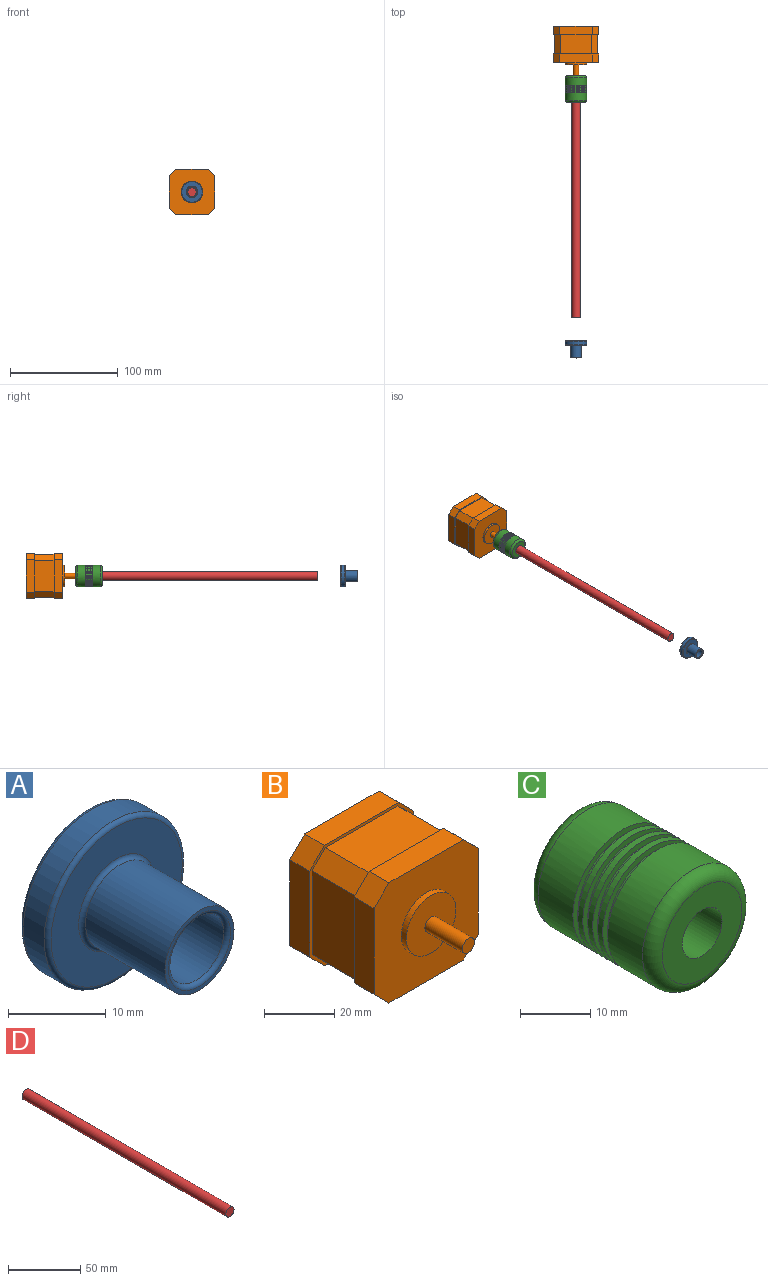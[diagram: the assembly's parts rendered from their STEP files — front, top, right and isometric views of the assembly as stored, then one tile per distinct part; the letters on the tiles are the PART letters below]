
ASSEMBLY  parts=4 mates=3
PART A: 10 faces, bbox 21.6x16x21.6 mm
  f0: cylinder r=4mm len=15.5mm, axis (0,-1,0), area 389.6mm2, adj f1,f9
  f1: plane 19x19mm, normal (0,1,0), area 233.3mm2, adj f0,f6
  f2: cylinder r=10mm len=20mm, axis (0,-1,0), area 188.5mm2, adj f6,f7
  f3: plane 19x19mm, normal (0,-1,0), area 188.5mm2, adj f7,f8
  f4: cylinder r=5mm len=11.5mm, axis (0,-1,0), area 361.3mm2, adj f5,f8
  f5: plane 10x10mm, normal (0,-1,0), area 14.9mm2, adj f4,f9
  f6: torus R=9.5mm, axis (0,-1,0), area 48.5mm2, adj f1,f2
  f7: torus R=9.5mm, axis (0,-1,0), area 48.5mm2, adj f2,f3
  f8: torus R=5.5mm, axis (0,-1,0), area 25.6mm2, adj f3,f4
  f9: torus R=4.5mm, axis (0,-1,0), area 20.6mm2, adj f0,f5
PART B: 32 faces, bbox 42x51x42 mm
  f0: plane 30x8mm, normal (0,0,-1), area 240mm2, adj f2,f3,f8,f18
  f1: plane 30x8mm, normal (1,0,0), area 240mm2, adj f3,f5,f8,f18
  f2: plane 8x6mm, normal (-0.71,0,-0.71), area 67.9mm2, adj f0,f6,f8,f18
  f3: plane 8x6mm, normal (0.71,0,-0.71), area 67.9mm2, adj f0,f1,f8,f18
  f4: plane 8x6mm, normal (-0.71,0,0.71), area 67.9mm2, adj f6,f7,f8,f18
  f5: plane 8x6mm, normal (0.71,0,0.71), area 67.9mm2, adj f1,f7,f8,f18
  f6: plane 30x8mm, normal (-1,0,0), area 240mm2, adj f2,f4,f8,f18
  f7: plane 30x8mm, normal (0,0,1), area 240mm2, adj f4,f5,f8,f18
  f8: plane 42x42mm, normal (0,-1,0), area 1377.8mm2, adj f0,f1,f2,f3,f4,f5,f6,f7
  f9: plane 18x5.41mm, normal (-0.71,0,0.71), area 137.8mm2, adj f10,f16,f17,f18
  f10: plane 29.17x18mm, normal (0,0,1), area 525.1mm2, adj f9,f11,f17,f18
  f11: plane 18x5.41mm, normal (0.71,0,0.71), area 137.8mm2, adj f10,f12,f17,f18
  f12: plane 29.17x18mm, normal (1,0,0), area 525.1mm2, adj f11,f13,f17,f18
  f13: plane 18x5.41mm, normal (0.71,0,-0.71), area 137.8mm2, adj f12,f14,f17,f18
  f14: plane 29.17x18mm, normal (0,0,-1), area 525.1mm2, adj f13,f15,f17,f18
  f15: plane 18x5.41mm, normal (-0.71,0,-0.71), area 137.8mm2, adj f14,f16,f17,f18
  f16: plane 29.17x18mm, normal (-1,0,0), area 525.1mm2, adj f9,f15,f17,f18
  f17: plane 42x42mm, normal (0,-1,0), area 150.6mm2, adj f9,f10,f11,f12,f13,f14,f15,f16
  f18: plane 42x42mm, normal (0,1,0), area 150.6mm2, adj f0,f1,f2,f3,f4,f5,f6,f7
  f19: plane 42x42mm, normal (0,1,0), area 1692mm2, adj f20,f21,f22,f23,f24,f25,f26,f27
  f20: plane 8x6mm, normal (-0.71,0,0.71), area 67.9mm2, adj f17,f19,f22,f27
  f21: plane 8x6mm, normal (0.71,0,0.71), area 67.9mm2, adj f17,f19,f22,f24
  f22: plane 30x8mm, normal (0,0,1), area 240mm2, adj f17,f19,f20,f21
  f23: plane 8x6mm, normal (0.71,0,-0.71), area 67.9mm2, adj f17,f19,f24,f26
  f24: plane 30x8mm, normal (1,0,0), area 240mm2, adj f17,f19,f21,f23
  f25: plane 8x6mm, normal (-0.71,0,-0.71), area 67.9mm2, adj f17,f19,f26,f27
  f26: plane 30x8mm, normal (0,0,-1), area 240mm2, adj f17,f19,f23,f25
  f27: plane 30x8mm, normal (-1,0,0), area 240mm2, adj f17,f19,f20,f25
  f28: cylinder r=10mm len=20mm, axis (0,1,0), area 125.7mm2, adj f8,f29
  f29: plane 20x20mm, normal (0,-1,0), area 294.5mm2, adj f28,f30
  f30: cylinder r=2.5mm len=15mm, axis (0,1,0), area 235.6mm2, adj f29,f31
  f31: plane 5x5mm, normal (0,-1,0), area 19.6mm2, adj f30
PART C: 24 faces, bbox 21.6x25x21.6 mm
  f0: cylinder r=2.5mm len=5mm, axis (0,-1,0), area 78.5mm2, adj f3,f22
  f1: cylinder r=10mm len=20mm, axis (0,-1,0), area 439.8mm2, adj f7,f21
  f2: cylinder r=10mm len=20mm, axis (0,-1,0), area 439.8mm2, adj f17,f20
  f3: plane 16x16mm, normal (0,1,0), area 181.4mm2, adj f0,f21
  f4: plane 16x16mm, normal (0,-1,0), area 150.8mm2, adj f20,f23
  f5: plane 20x20mm, normal (0,1,0), area 59.7mm2, adj f6,f8
  f6: cylinder r=9mm len=18mm, axis (0,1,0), area 56.5mm2, adj f5,f7
  f7: plane 20x20mm, normal (0,-1,0), area 59.7mm2, adj f1,f6
  f8: cylinder r=10mm len=20mm, axis (0,-1,0), area 62.8mm2, adj f5,f11
  f9: plane 20x20mm, normal (0,1,0), area 59.7mm2, adj f10,f12
  f10: cylinder r=9mm len=18mm, axis (0,1,0), area 56.5mm2, adj f9,f11
  f11: plane 20x20mm, normal (0,-1,0), area 59.7mm2, adj f8,f10
  f12: cylinder r=10mm len=20mm, axis (0,-1,0), area 62.8mm2, adj f9,f15
  f13: plane 20x20mm, normal (0,1,0), area 59.7mm2, adj f14,f16
  f14: cylinder r=9mm len=18mm, axis (0,1,0), area 56.5mm2, adj f13,f15
  f15: plane 20x20mm, normal (0,-1,0), area 59.7mm2, adj f12,f14
  f16: cylinder r=10mm len=20mm, axis (0,-1,0), area 62.8mm2, adj f13,f19
  f17: plane 20x20mm, normal (0,1,0), area 59.7mm2, adj f2,f18
  f18: cylinder r=9mm len=18mm, axis (0,1,0), area 56.5mm2, adj f17,f19
  f19: plane 20x20mm, normal (0,-1,0), area 59.7mm2, adj f16,f18
  f20: torus R=8mm, axis (0,-1,0), area 183mm2, adj f2,f4
  f21: torus R=8mm, axis (0,-1,0), area 183mm2, adj f1,f3
  f22: plane 8x8mm, normal (0,-1,0), area 30.6mm2, adj f0,f23
  f23: cylinder r=4mm len=20mm, axis (0,-1,0), area 502.7mm2, adj f4,f22
PART D: 3 faces, bbox 8x200x8 mm
  f0: cylinder r=4mm len=200mm, axis (0,-1,0), area 5026.5mm2, adj f1,f2
  f1: plane 8x8mm, normal (0,1,0), area 50.3mm2, adj f0
  f2: plane 8x8mm, normal (0,-1,0), area 50.3mm2, adj f0
PLACE A t=(0,-258.45,0)mm
PLACE B at identity fixed
PLACE C t=(0,-37,0)mm
PLACE D t=(0,-237,0)mm
MATE fastened C.f23 <-> D.f0  axis (0,-1,0) through (0,-37,0)mm
MATE slider A.f0 <-> D.f0  axis (0,-1,0) through (0,-273.95,0)mm
MATE fastened B.f30 <-> C.f0  axis (0,-1,0) through (0,-17,0)mm
